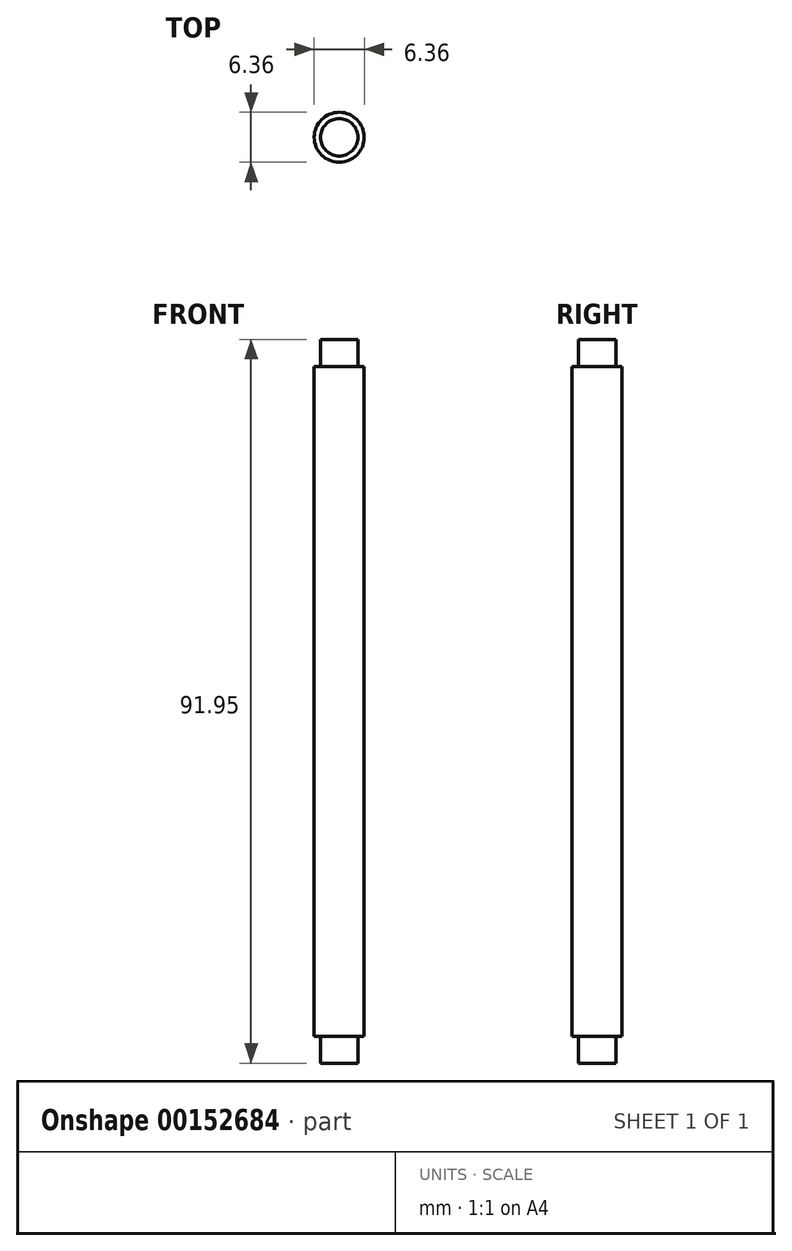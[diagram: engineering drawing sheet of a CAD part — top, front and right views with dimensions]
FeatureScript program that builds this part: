
annotation { "Feature Type Name" : "Feature", "Feature Type Description" : "" }
export const myFeature = defineFeature(function(context is Context, id is Id, definition is map)
    precondition{}
    {
        {
            var Q0;
            Q0=qCreatedBy(makeId("Top.planeOp"),FACE);
            var sketch = newSketch(context, id + "F0", { "sketchPlane" : qUnion([Q0])});
            skCircle(sketch, "E0", {"center": v(0, 0) * mm, "radius": 3.18 * mm});
            skSolve(sketch);
        }
        {
            var Q0;
            Q0 = qSketchRegion(id + "F0", true);
            extrude(context, id + "F1", {"entities" : qUnion([Q0]), "depth" : 85.12 * mm});
        }
        {
            var Q0;
            Q0=makeQuery(id+"F1.opExtrude","CAP_FACE",FACE,{"disambiguationData":[OSD([sQuery(id+"F0.wireOp",EDGE,"E0")])],"isStart":true});
            cPlane(context, id + "F2", {"entities" : qUnion([Q0]), "cplaneType" : CPlaneType.OFFSET, "offset" : 3.42 * mm, "width" : 152.4 * mm, "height" : 152.4 * mm});
        }
        {
            var Q0;
            Q0=makeQuery(id+"F1.opExtrude","CAP_FACE",FACE,{"disambiguationData":[OSD([sQuery(id+"F0.wireOp",EDGE,"E0")])],"isStart":false});
            var sketch = newSketch(context, id + "F3", { "sketchPlane" : qUnion([Q0])});
            skCircle(sketch, "E1", {"center": v(0, 0) * mm, "radius": 2.38 * mm});
            skSolve(sketch);
        }
        {
            var Q0;
            Q0 = qSketchRegion(id + "F3", true);
            var Q1;
            Q1=qCreatedBy(id+"F2.planeOp",FACE);
            extrude(context, id + "F4", {"entities" : qUnion([Q0]), "operationType" : NewBodyOperationType.ADD, "depth" : 3.42 * mm, "hasSecondDirection" : true, "secondDirectionBound" : SecondDirectionBoundingType.UP_TO_SURFACE, "secondDirectionOppositeDirection" : true, "secondDirectionBoundEntityFace" : qUnion([Q1]), "secondDirectionDepth" : 25.4 * mm});
        }
    });
